# Revit family: Fireplace_Gas_HeatNGlo_Twilight
name_source: partatom
category: Mechanical Equipment
revit_build: Autodesk Revit 2015 (Build: 20140323_1530(x64)
units: mm (PartAtom-declared; Revit-internal decimal feet)

## types (4) — shared parameters
Air Infiltration = 0.07 cfm/ft^2
Assembly Code = D3020
Construction Details = http://www.arcat.com
Default Elevation = 0' - 0"
Efficiency Ratings = as Specified
Electrical_Voltage = 120 V
Fixture Finish = Metal - HeatNGlo - Metallic Black
Fuel Consumption = as Specified
HVAC_BTU Output = 0.0 Btu/h
Heating Capacity = as Specified
Keynote = 10305
Manufacturer = Heat & Glo
Manufacturer Website = http://www.heatnglo.com
Opening Height = 1' - 9 1/2"
Opening Width = 3' - 0 1/4"
Product Data = http://www.arcat.com
Revision = R2_2014-09
Sales Information = http://www.heatnglo.com
Send Message = http://www.arcat.com
Sound Transmission Class (STC) = 27
Specification = http://www.arcat.com
Standards Conformance = cULus
Structural Test Pressure = No Damage at 75 psf
URL = http://www.heatnglo.com
Unit Depth = 2' - 0"
Unit Height = 3' - 2 5/8"
Unit Width = 3' - 6"
Water Penetration = No Penetration at 8 and 25 psf
zero-valued in all types: Expected Lifespan (Years), Maintenance Schedule (Months), R-Value, Unit Weight, Warranty Duration (Years)

## per-type parameters (varying)
| type | Description | Fuel Type | HVAC_BTU Input | Model |
| 36x22 Viewing Area LP Modern | Heat & Glo Gas Burning Fireplace - Twilight Modern See-Thru as Specified | LP | 36000.0 Btu/h | TwilightLP-II-MOD |
| 36x22 Viewing Area NG Modern | Heat & Glo Gas Burning Fireplace - Twilight Modern See-Thru as Specified | NG | 38000.0 Btu/h | Twilight-II-MOD |
| 36x22 Viewing Area LP | Heat & Glo Gas Burning Fireplace - Twilight II See-Thru as Specified | LP | 36000.0 Btu/h | TwilightLP-II |
| 36x22 Viewing Area NG | Heat & Glo Gas Burning Fireplace - Twilight II See-Thru as Specified | NG | 38000.0 Btu/h | Twilight-II |

## geometry (parser evidence)
native form markers: Blend x10, Sweep x5
no freeform markers — native parametric forms only
